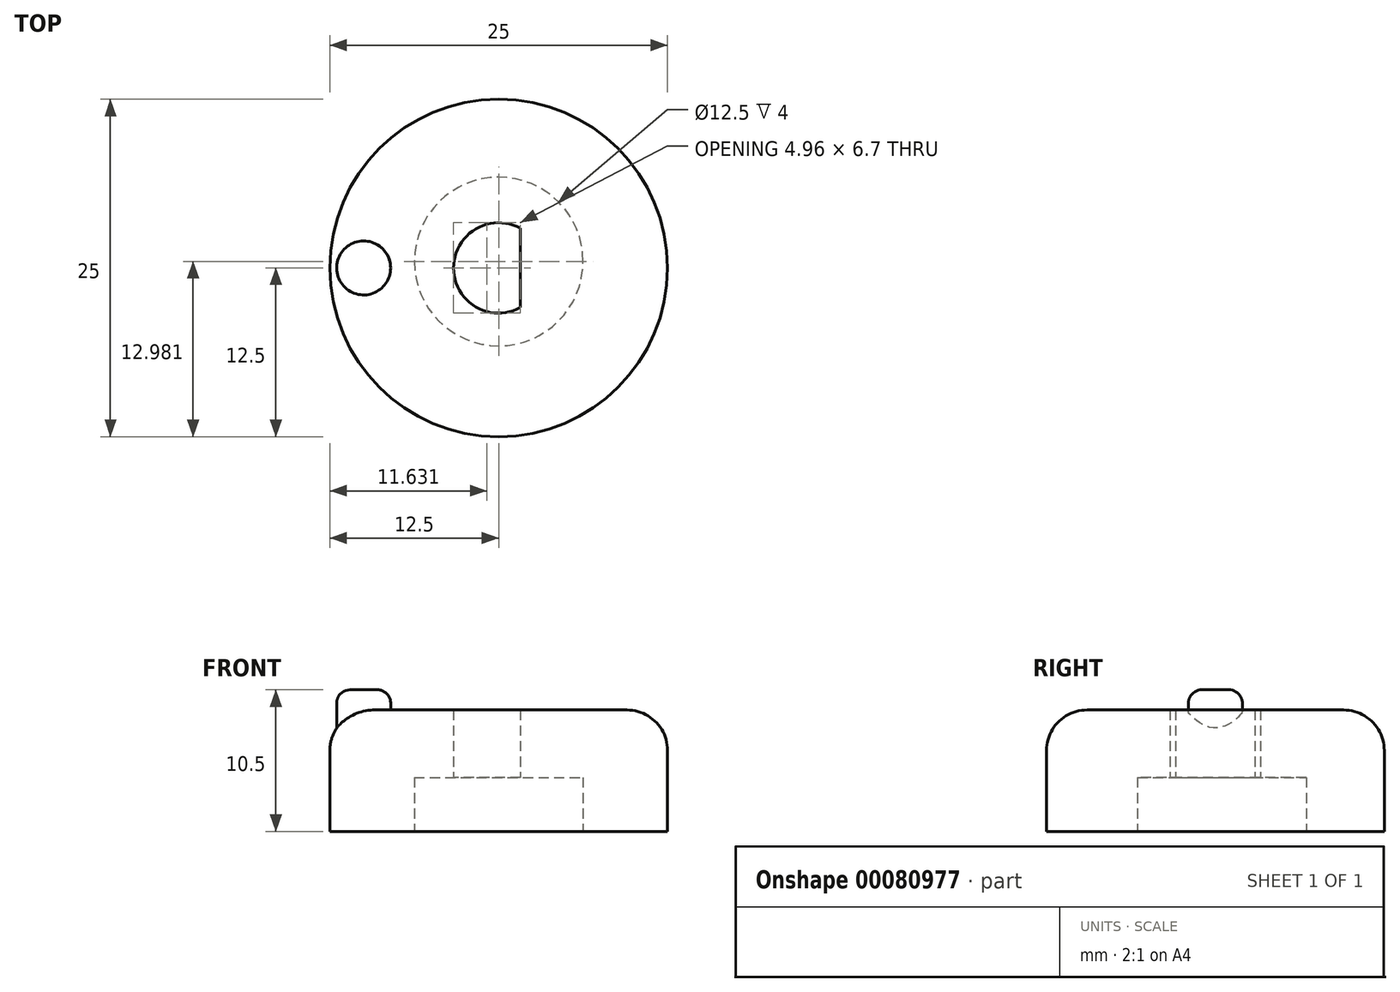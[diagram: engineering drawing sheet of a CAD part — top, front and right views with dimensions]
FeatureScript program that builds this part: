
annotation { "Feature Type Name" : "Feature", "Feature Type Description" : "" }
export const myFeature = defineFeature(function(context is Context, id is Id, definition is map)
    precondition{}
    {
        {
            var Q0;
            Q0=qCreatedBy(makeId("Top.planeOp"),FACE);
            var sketch = newSketch(context, id + "F0", { "sketchPlane" : qUnion([Q0])});
            skCircle(sketch, "E0", {"center": v(0, 0) * mm, "radius": 12.5 * mm});
            skArc(sketch, "E1", {"start": v(1.61, 2.94) * mm, "mid": v(-3.35, 0) * mm, "end": v(1.61, -2.94) * mm});
            skLineSegment(sketch, "E2", {"start": v(-3.35, 0) * mm, "end": v(1.61, 0) * mm});
            skPoint(sketch, "E3", {"position": v(1.61, 2.94) * mm});
            skLineSegment(sketch, "E4", {"start": v(1.61, 2.94) * mm, "end": v(1.61, -2.94) * mm});
            skSolve(sketch);
        }
        {
            var Q0;
            Q0=qSketchRegion(id+"F0",true);
            extrude(context, id + "F1", {"entities" : qUnion([Q0]), "depth" : 9 * mm});
        }
        {
            var Q0;
            Q0=makeQuery(id+"F1.opExtrude","CAP_FACE",FACE,{"disambiguationData":[OSD([sQuery(id+"F0.wireOp",EDGE,"E0"),sQuery(id+"F0.wireOp",EDGE,"E1"),sQuery(id+"F0.wireOp",EDGE,"E4")])],"isStart":true});
            var sketch = newSketch(context, id + "F2", { "sketchPlane" : qUnion([Q0])});
            skCircle(sketch, "E5", {"center": v(0, -0.48) * mm, "radius": 6.25 * mm});
            skSolve(sketch);
        }
        {
            var Q0;
            Q0=qSketchRegion(id+"F2",true);
            extrude(context, id + "F3", {"entities" : qUnion([Q0]), "operationType" : NewBodyOperationType.REMOVE, "oppositeDirection" : true, "depth" : 4 * mm});
        }
        {
            var Q0;
            Q0=makeQuery(id+"Fi9KlxCAU00Nf1F_1.boolean.opBoolean","MERGE",FACE,{"derivedFrom":[makeQuery(id+"F1.opExtrude","CAP_FACE",FACE,{"disambiguationData":[OSD([sQuery(id+"F0.wireOp",EDGE,"E0"),sQuery(id+"F0.wireOp",EDGE,"E1"),sQuery(id+"F0.wireOp",EDGE,"E4")])],"isStart":false}),makeQuery(id+"Fi9KlxCAU00Nf1F_1.opExtrude","CAP_FACE",FACE,{"disambiguationData":[OSD([sQuery(id+"Fyej4MUWWs5OMHl_1.wireOp",EDGE,"5d3b896b-8158-4870-abf8-989dcde11d84.0")])],"isStart":true})]});
            var sketch = newSketch(context, id + "F4", { "sketchPlane" : qUnion([Q0])});
            skCircle(sketch, "E6", {"center": v(-10, 0) * mm, "radius": 2 * mm});
            skLineSegment(sketch, "E7", {"start": v(-10, 0) * mm, "end": v(0, 0) * mm});
            skSolve(sketch);
        }
        {
            var Q0;
            Q0=makeQuery(id+"F4.imprint","IMPRINT",FACE,{"disambiguationData":[TD([[makeQuery(id+"F4.imprint","IMPRINT",EDGE,{"derivedFrom":sQuery(id+"F4.wireOp",EDGE,"E6")}),1.0]])]});
            extrude(context, id + "F5", {"entities" : qUnion([Q0]), "operationType" : NewBodyOperationType.ADD, "depth" : 1.5 * mm});
        }
        {
            var Q0;
            Q0=makeQuery(id+"F5.opExtrude","CAP_EDGE",EDGE,{"disambiguationData":[OSD([sQuery(id+"F4.wireOp",EDGE,"E6")])],"isStart":false});
            fillet(context, id + "F6", {"entities" : qUnion([Q0]), "radius" : 1 * mm, "tangentPropagation" : true, "allowEdgeOverflow" : false});
        }
        {
            var Q0;
            Q0=makeQuery(id+"F1.opExtrude","CAP_EDGE",EDGE,{"disambiguationData":[OSD([sQuery(id+"F0.wireOp",EDGE,"E0")])],"isStart":false});
            fillet(context, id + "F7", {"entities" : qUnion([Q0]), "radius" : 3 * mm, "tangentPropagation" : true, "allowEdgeOverflow" : false});
        }
    });
